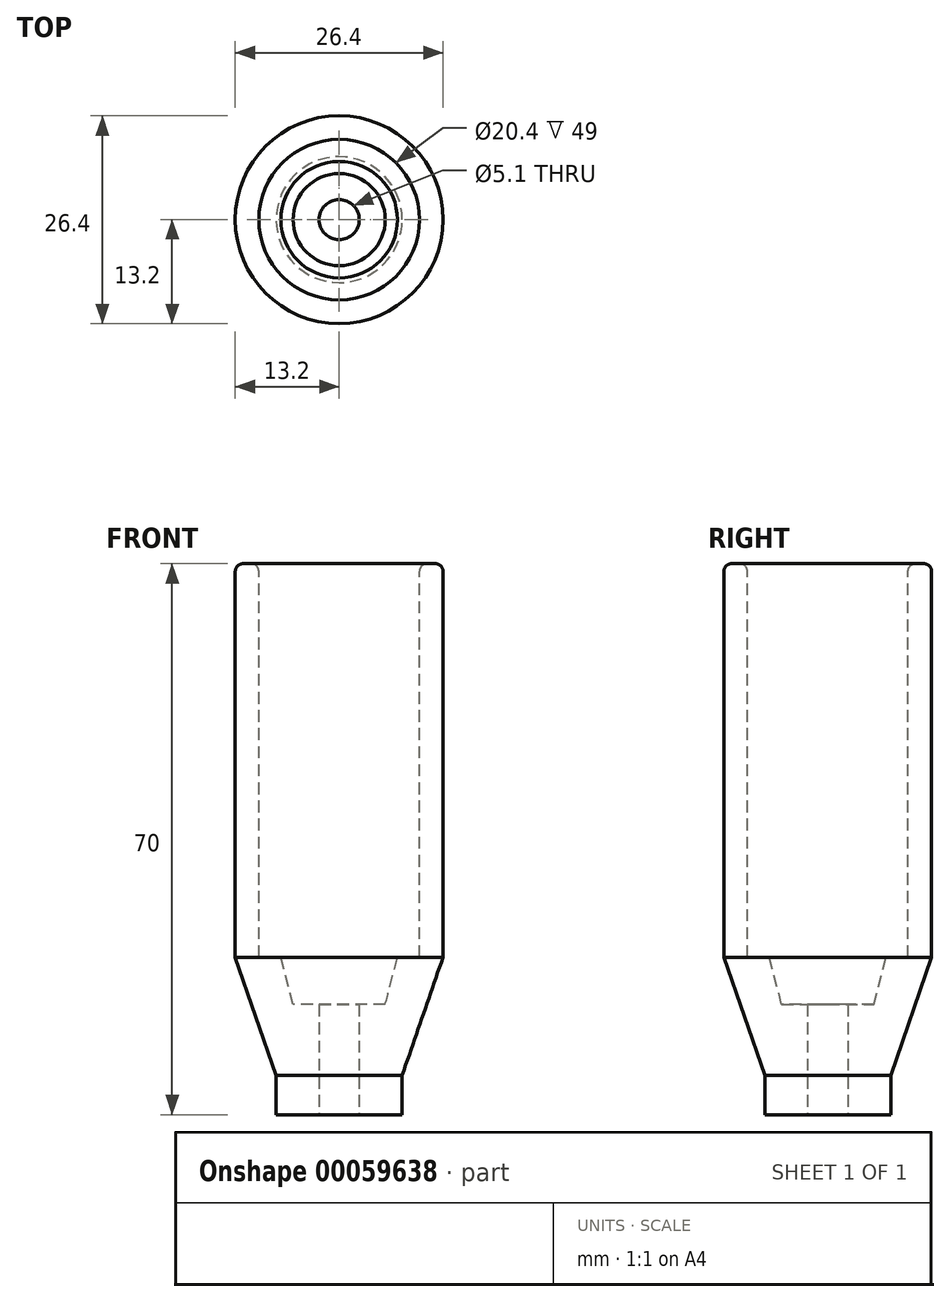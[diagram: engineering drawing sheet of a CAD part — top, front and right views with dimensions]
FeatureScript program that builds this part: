
annotation { "Feature Type Name" : "Feature", "Feature Type Description" : "" }
export const myFeature = defineFeature(function(context is Context, id is Id, definition is map)
    precondition{}
    {
        {
            var Q0;
            Q0=qCreatedBy(makeId("Front.planeOp"),FACE);
            var sketch = newSketch(context, id + "F0", { "sketchPlane" : qUnion([Q0])});
            skLineSegment(sketch, "E0", {"start": v(0, 65.84) * mm, "end": v(0, -61.8) * mm, "construction": true});
            skLineSegment(sketch, "E1", {"start": v(0, 61.34) * mm, "end": v(-10.2, 61.34) * mm, "construction": true});
            skLineSegment(sketch, "E2", {"start": v(-13.2, 61.34) * mm, "end": v(-13.2, 11.34) * mm});
            skLineSegment(sketch, "E3", {"start": v(-13.2, 11.34) * mm, "end": v(-8, -3.66) * mm});
            skLineSegment(sketch, "E4", {"start": v(-8, -3.66) * mm, "end": v(-8, -8.66) * mm});
            skLineSegment(sketch, "E5", {"start": v(-8, -8.66) * mm, "end": v(0, -8.66) * mm});
            skLineSegment(sketch, "E6", {"start": v(-10.2, 11.34) * mm, "end": v(-10.2, 61.34) * mm});
            skLineSegment(sketch, "E7", {"start": v(-5.85, 5.34) * mm, "end": v(-2.77, -3.55) * mm, "construction": true});
            skLineSegment(sketch, "E8", {"start": v(-10.2, 61.34) * mm, "end": v(-13.2, 61.34) * mm});
            skLineSegment(sketch, "E9", {"start": v(-5.85, 5.34) * mm, "end": v(0, 5.34) * mm});
            skLineSegment(sketch, "E10", {"start": v(0, -8.66) * mm, "end": v(0, 5.34) * mm});
            skLineSegment(sketch, "E11", {"start": v(-10.2, 11.34) * mm, "end": v(-7.4, 11.34) * mm});
            skLineSegment(sketch, "E12", {"start": v(-7.4, 11.34) * mm, "end": v(-5.85, 5.34) * mm});
            skSolve(sketch);
        }
        {
            var Q0;
            Q0=makeQuery(id+"F0.imprint","IMPRINT",FACE,{"disambiguationData":[TD([[makeQuery(id+"F0.imprint","IMPRINT",EDGE,{"derivedFrom":sQuery(id+"F0.wireOp",EDGE,"E2")}),1.0]])]});
            var Q1;
            Q1=sQuery(id+"F0.wireOp",EDGE,"E2");
            var Q2;
            Q2=sQuery(id+"F0.wireOp",EDGE,"E6");
            var Q3;
            Q3=sQuery(id+"F0.wireOp",EDGE,"E8");
            var Q4;
            Q4=sQuery(id+"F0.wireOp",EDGE,"E3");
            var Q5;
            Q5=sQuery(id+"F0.wireOp",EDGE,"hLR8M1aP-WHKg-m9Wu-bzxs-W95oanOhnAe0");
            var Q6;
            Q6=sQuery(id+"F0.wireOp",EDGE,"E9");
            var Q7;
            Q7=sQuery(id+"F0.wireOp",EDGE,"E4");
            var Q8;
            Q8=sQuery(id+"F0.wireOp",EDGE,"E5");
            var Q9;
            Q9=sQuery(id+"F0.wireOp",EDGE,"E0");
            revolve(context, id + "F1", {"entities" : qUnion([Q0]), "surfaceEntities" : qUnion([Q1, Q2, Q3, Q4, Q5, Q6, Q7, Q8]), "axis" : qUnion([Q9]), "revolveType" : RevolveType.SYMMETRIC, "angle" : 360 * degree});
        }
        {
            var Q0;
            Q0=makeQuery(id+"F1.opRevolve","SWEPT_EDGE",EDGE,{"disambiguationData":[OSD([sQuery(id+"F0.wireOp",EDGE,"E2"),sQuery(id+"F0.wireOp",EDGE,"E8")])]});
            var Q1;
            Q1=makeQuery(id+"F1.opRevolve","SWEPT_EDGE",EDGE,{"disambiguationData":[OSD([sQuery(id+"F0.wireOp",EDGE,"E6"),sQuery(id+"F0.wireOp",EDGE,"E8")])]});
            fillet(context, id + "F2", {"entities" : qUnion([Q0, Q1]), "radius" : 1 * mm, "tangentPropagation" : true, "allowEdgeOverflow" : false});
        }
        {
            var Q0;
            Q0=makeQuery(id+"F1.opRevolve","SWEPT_FACE",FACE,{"disambiguationData":[OSD([sQuery(id+"F0.wireOp",EDGE,"E5")])]});
            var sketch = newSketch(context, id + "F3", { "sketchPlane" : qUnion([Q0])});
            skPoint(sketch, "E13", {"position": v(0, 0) * mm});
            skSolve(sketch);
        }
        {
            var Q0;
            Q0=sQuery(id+"F3.wireOp",VERTEX,"E13");
            var Q1;
            Q1=makeQuery(id+"F1.opRevolve","SWEPT_BODY",BODY,{"disambiguationData":[OSD([sQuery(id+"F0.wireOp",EDGE,"E2"),sQuery(id+"F0.wireOp",EDGE,"E3"),sQuery(id+"F0.wireOp",EDGE,"E4"),sQuery(id+"F0.wireOp",EDGE,"E5"),sQuery(id+"F0.wireOp",EDGE,"E6"),sQuery(id+"F0.wireOp",EDGE,"hLR8M1aP-WHKg-m9Wu-bzxs-W95oanOhnAe0"),sQuery(id+"F0.wireOp",EDGE,"E8"),sQuery(id+"F0.wireOp",EDGE,"E9"),sQuery(id+"F0.wireOp",EDGE,"E10")])]});
            hole(context, id + "F4", {"style" : HoleStyle.SIMPLE, "holeDiameter" : 5.1 * mm, "endStyle" : HoleEndStyle.THROUGH, "locations" : qUnion([Q0]), "scope" : qUnion([Q1])});
        }
    });
